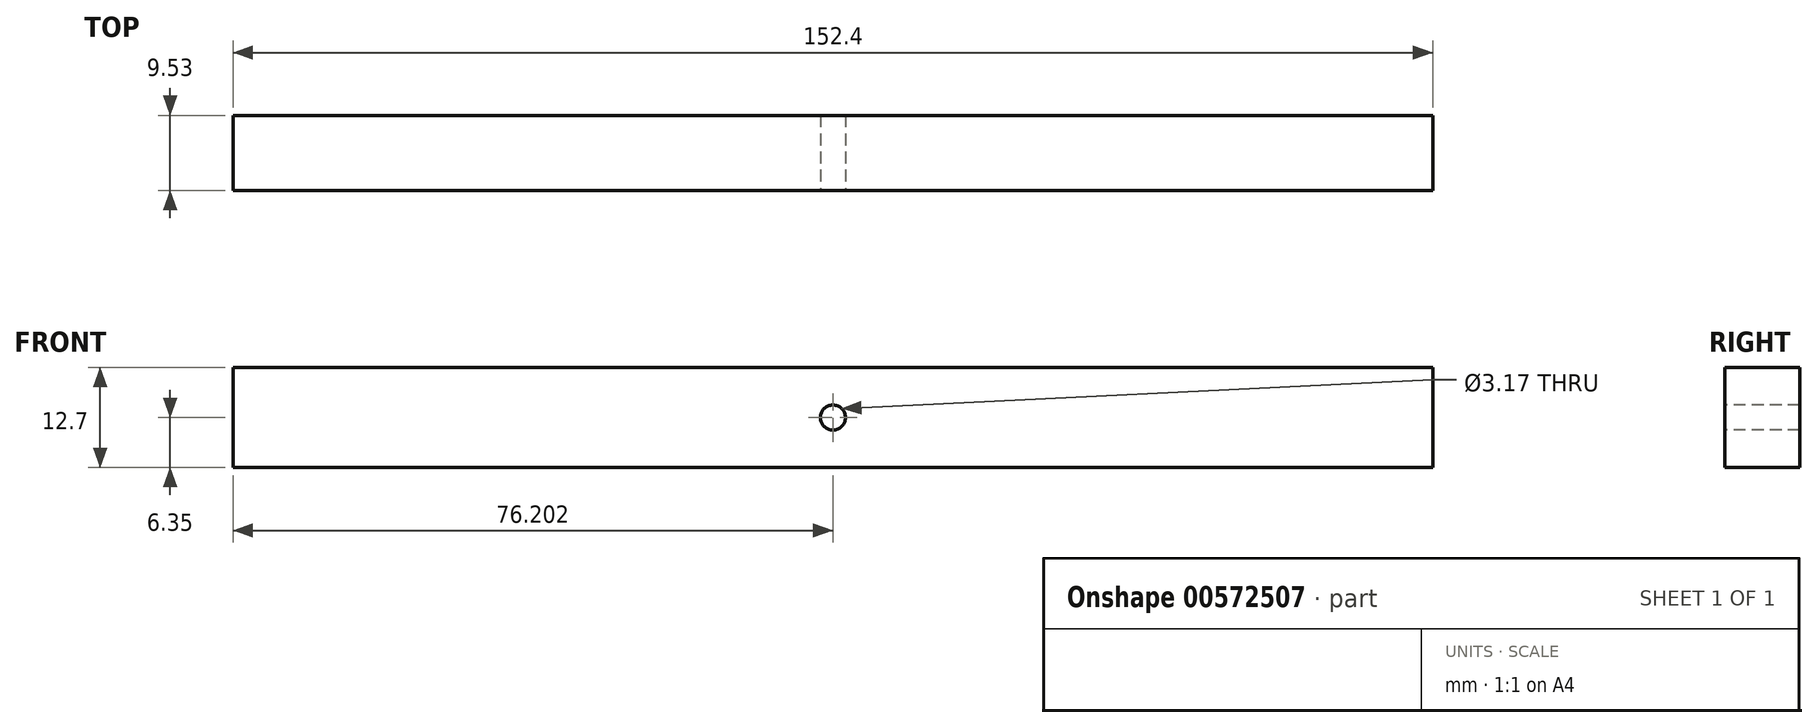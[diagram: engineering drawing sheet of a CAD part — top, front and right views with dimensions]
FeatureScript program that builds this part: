
annotation { "Feature Type Name" : "Feature", "Feature Type Description" : "" }
export const myFeature = defineFeature(function(context is Context, id is Id, definition is map)
    precondition{}
    {
        {
            var Q0;
            Q0=qCreatedBy(makeId("Top.planeOp"),FACE);
            var sketch = newSketch(context, id + "F0", { "sketchPlane" : qUnion([Q0])});
            skLineSegment(sketch, "E0.bottom", {"start": v(-60.08, 9.52) * mm, "end": v(92.32, 9.52) * mm});
            skLineSegment(sketch, "E0.top", {"start": v(-60.08, 0) * mm, "end": v(92.32, 0) * mm});
            skLineSegment(sketch, "E0.left", {"start": v(-60.08, 9.52) * mm, "end": v(-60.08, 0) * mm});
            skLineSegment(sketch, "E0.right", {"start": v(92.32, 9.52) * mm, "end": v(92.32, 0) * mm});
            skSolve(sketch);
        }
        {
            var Q0;
            Q0=makeQuery(id+"F0.imprint","IMPRINT",FACE,{"disambiguationData":[TD([[makeQuery(id+"F0.imprint","IMPRINT",EDGE,{"derivedFrom":sQuery(id+"F0.wireOp",EDGE,"E0.bottom")}),-1.0]])]});
            extrude(context, id + "F1", {"entities" : qUnion([Q0]), "depth" : 12.7 * mm, "offsetDistance" : 25.4 * mm});
        }
        {
            var Q0;
            Q0=makeQuery(id+"F1.opExtrude","SWEPT_FACE",FACE,{"disambiguationData":[OSD([sQuery(id+"F0.wireOp",EDGE,"E0.top")])]});
            var sketch = newSketch(context, id + "F2", { "sketchPlane" : qUnion([Q0])});
            skCircle(sketch, "E1", {"center": v(16.12, 6.35) * mm, "radius": 1.59 * mm});
            skPoint(sketch, "E1.centerSnap0", {"position": v(-60.08, 6.35) * mm});
            skPoint(sketch, "E1.centerSnap1", {"position": v(16.12, 12.7) * mm});
            skSolve(sketch);
        }
        {
            var Q0;
            Q0=makeQuery(id+"F2.imprint","IMPRINT",FACE,{"disambiguationData":[TD([[makeQuery(id+"F2.imprint","IMPRINT",EDGE,{"derivedFrom":sQuery(id+"F2.wireOp",EDGE,"E1")}),1.0]])]});
            extrude(context, id + "F3", {"entities" : qUnion([Q0]), "operationType" : NewBodyOperationType.REMOVE, "oppositeDirection" : true, "depth" : 25.4 * mm, "offsetDistance" : 25.4 * mm});
        }
    });
